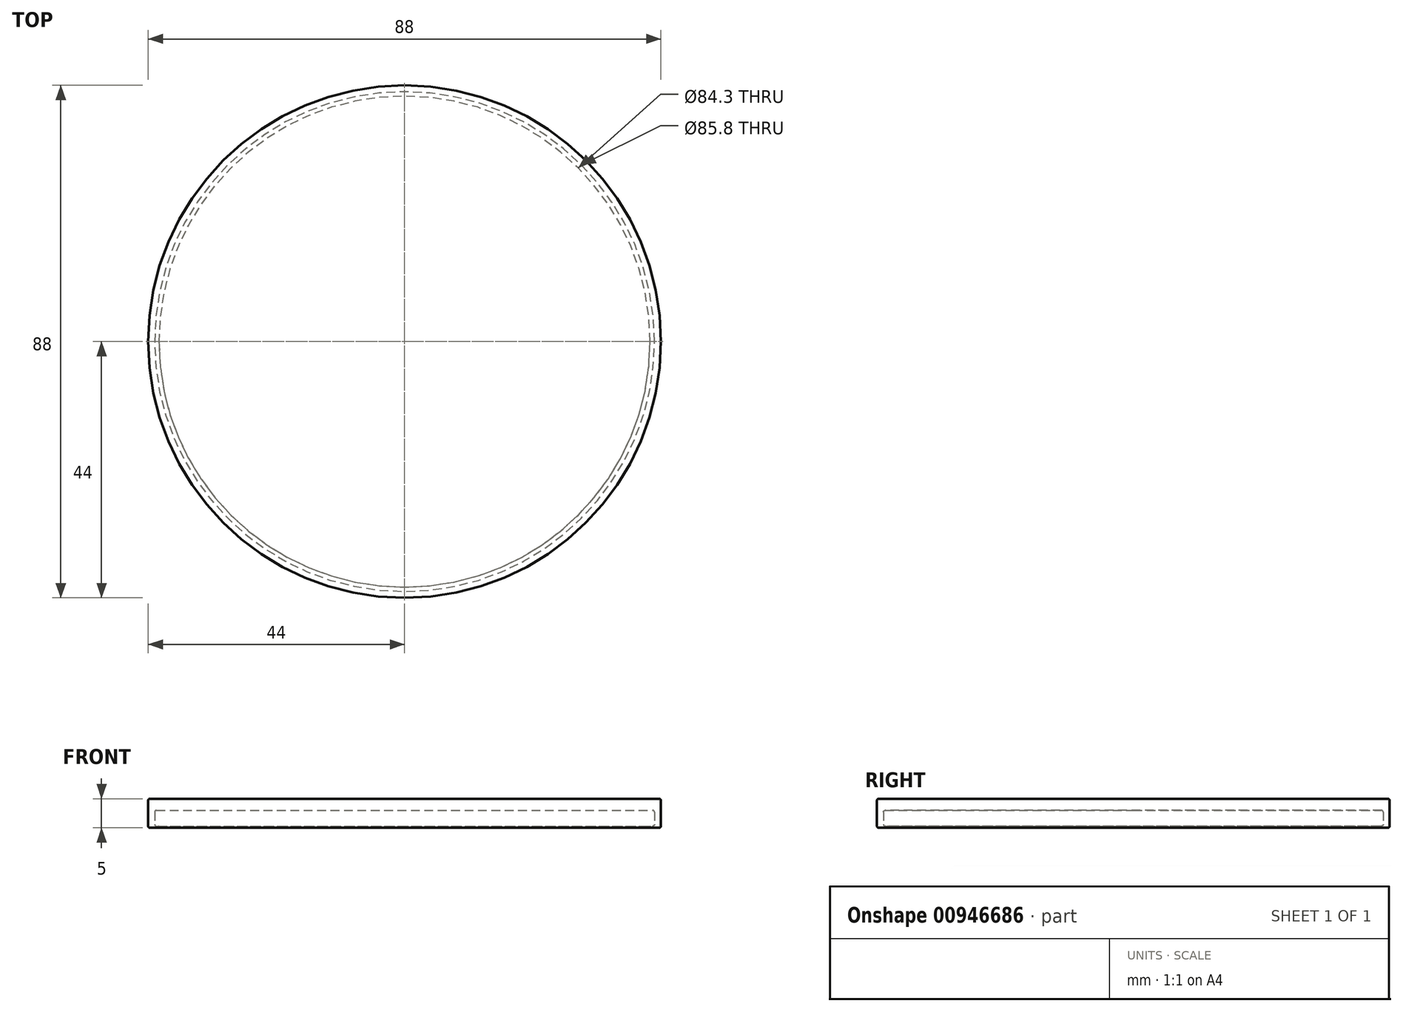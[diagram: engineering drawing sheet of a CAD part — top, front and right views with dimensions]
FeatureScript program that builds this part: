
annotation { "Feature Type Name" : "Feature", "Feature Type Description" : "" }
export const myFeature = defineFeature(function(context is Context, id is Id, definition is map)
    precondition{}
    {
        {
            var Q0;
            Q0=qCreatedBy(makeId("Top.planeOp"),FACE);
            var sketch = newSketch(context, id + "F0", { "sketchPlane" : qUnion([Q0])});
            skCircle(sketch, "E0", {"center": v(0, 0) * mm, "radius": 42.9 * mm});
            skCircle(sketch, "E1", {"center": v(0, 0) * mm, "radius": 44 * mm});
            skCircle(sketch, "E2", {"center": v(0, 0) * mm, "radius": 42.25 * mm});
            skSolve(sketch);
        }
        {
            var Q0;
            Q0=makeQuery(id+"F0.imprint","IMPRINT",FACE,{"disambiguationData":[TD([[makeQuery(id+"F0.imprint","IMPRINT",EDGE,{"derivedFrom":sQuery(id+"F0.wireOp",EDGE,"E2")}),1.0]])]});
            var Q1;
            Q1=makeQuery(id+"F0.imprint","IMPRINT",FACE,{"disambiguationData":[TD([[makeQuery(id+"F0.imprint","IMPRINT",EDGE,{"derivedFrom":sQuery(id+"F0.wireOp",EDGE,"E0")}),1.0]])]});
            var Q2;
            Q2=makeQuery(id+"F0.imprint","IMPRINT",FACE,{"disambiguationData":[TD([[makeQuery(id+"F0.imprint","IMPRINT",EDGE,{"derivedFrom":sQuery(id+"F0.wireOp",EDGE,"E0")}),-1.0]])]});
            var Q3;
            Q3=sQuery(id+"F0.wireOp",EDGE,"E1");
            var Q4;
            Q4=sQuery(id+"F0.wireOp",EDGE,"E0");
            var Q5;
            Q5=sQuery(id+"F0.wireOp",EDGE,"E2");
            extrude(context, id + "F1", {"entities" : qUnion([Q0, Q1, Q2]), "surfaceEntities" : qUnion([Q3, Q4, Q5]), "depth" : 5 * mm, "offsetDistance" : 25 * mm});
        }
        {
            var Q0;
            Q0=makeQuery(id+"F1.opExtrude","CAP_FACE",FACE,{"disambiguationData":[OSD([sQuery(id+"F0.wireOp",EDGE,"E1")])],"isStart":true});
            var sketch = newSketch(context, id + "F2", { "sketchPlane" : qUnion([Q0])});
            skCircle(sketch, "E3", {"center": v(0, 0) * mm, "radius": 42.9 * mm});
            skSolve(sketch);
        }
        {
            var Q0;
            Q0=makeQuery(id+"F2.imprint","IMPRINT",FACE,{"disambiguationData":[TD([[makeQuery(id+"F2.imprint","IMPRINT",EDGE,{"derivedFrom":sQuery(id+"F2.wireOp",EDGE,"E3")}),1.0]])]});
            extrude(context, id + "F3", {"entities" : qUnion([Q0]), "operationType" : NewBodyOperationType.REMOVE, "oppositeDirection" : true, "depth" : 3 * mm, "offsetDistance" : 25 * mm});
        }
        {
            var Q0;
            Q0=makeQuery(id+"F1.opExtrude","CAP_FACE",FACE,{"disambiguationData":[OSD([sQuery(id+"F0.wireOp",EDGE,"E1")])],"isStart":true});
            var sketch = newSketch(context, id + "F4", { "sketchPlane" : qUnion([Q0])});
            skCircle(sketch, "E4", {"center": v(0, 0) * mm, "radius": 42.15 * mm});
            skCircle(sketch, "E5", {"center": v(0, 0) * mm, "radius": 42.9 * mm});
            skSolve(sketch);
        }
        {
            var Q0;
            Q0=makeQuery(id+"F4.imprint","IMPRINT",FACE,{"disambiguationData":[TD([[makeQuery(id+"F4.imprint","IMPRINT",EDGE,{"derivedFrom":sQuery(id+"F4.wireOp",EDGE,"E4")}),-1.0]])]});
            var Q1;
            Q1=sQuery(id+"F4.wireOp",EDGE,"E4");
            var Q2;
            Q2=sQuery(id+"F4.wireOp",EDGE,"E5");
            extrude(context, id + "F5", {"entities" : qUnion([Q0]), "operationType" : NewBodyOperationType.ADD, "surfaceEntities" : qUnion([Q1, Q2]), "oppositeDirection" : true, "depth" : .3 * mm, "offsetDistance" : 25 * mm});
        }
        {
            var Q0;
            Q0=makeQuery(id+"F3.boolean.opBoolean","COPY",FACE,{"derivedFrom":makeQuery(id+"F3.opExtrude","SWEPT_FACE",FACE,{"disambiguationData":[OSD([sQuery(id+"F2.wireOp",EDGE,"E3")])]})});
            var Q1;
            Q1=makeQuery(id+"F1.opExtrude","SWEPT_FACE",FACE,{"disambiguationData":[OSD([sQuery(id+"F0.wireOp",EDGE,"E1")])]});
            fillet(context, id + "F6", {"entities" : qUnion([Q0, Q1]), "radius" : .3 * mm, "tangentPropagation" : true, "allowEdgeOverflow" : false});
        }
        {
            var Q0;
            Q0=makeQuery(id+"F5.opExtrude","SWEPT_FACE",FACE,{"disambiguationData":[OSD([sQuery(id+"F4.wireOp",EDGE,"E4")])]});
            fillet(context, id + "F7", {"entities" : qUnion([Q0]), "radius" : .1 * mm, "tangentPropagation" : true, "allowEdgeOverflow" : false});
        }
    });
